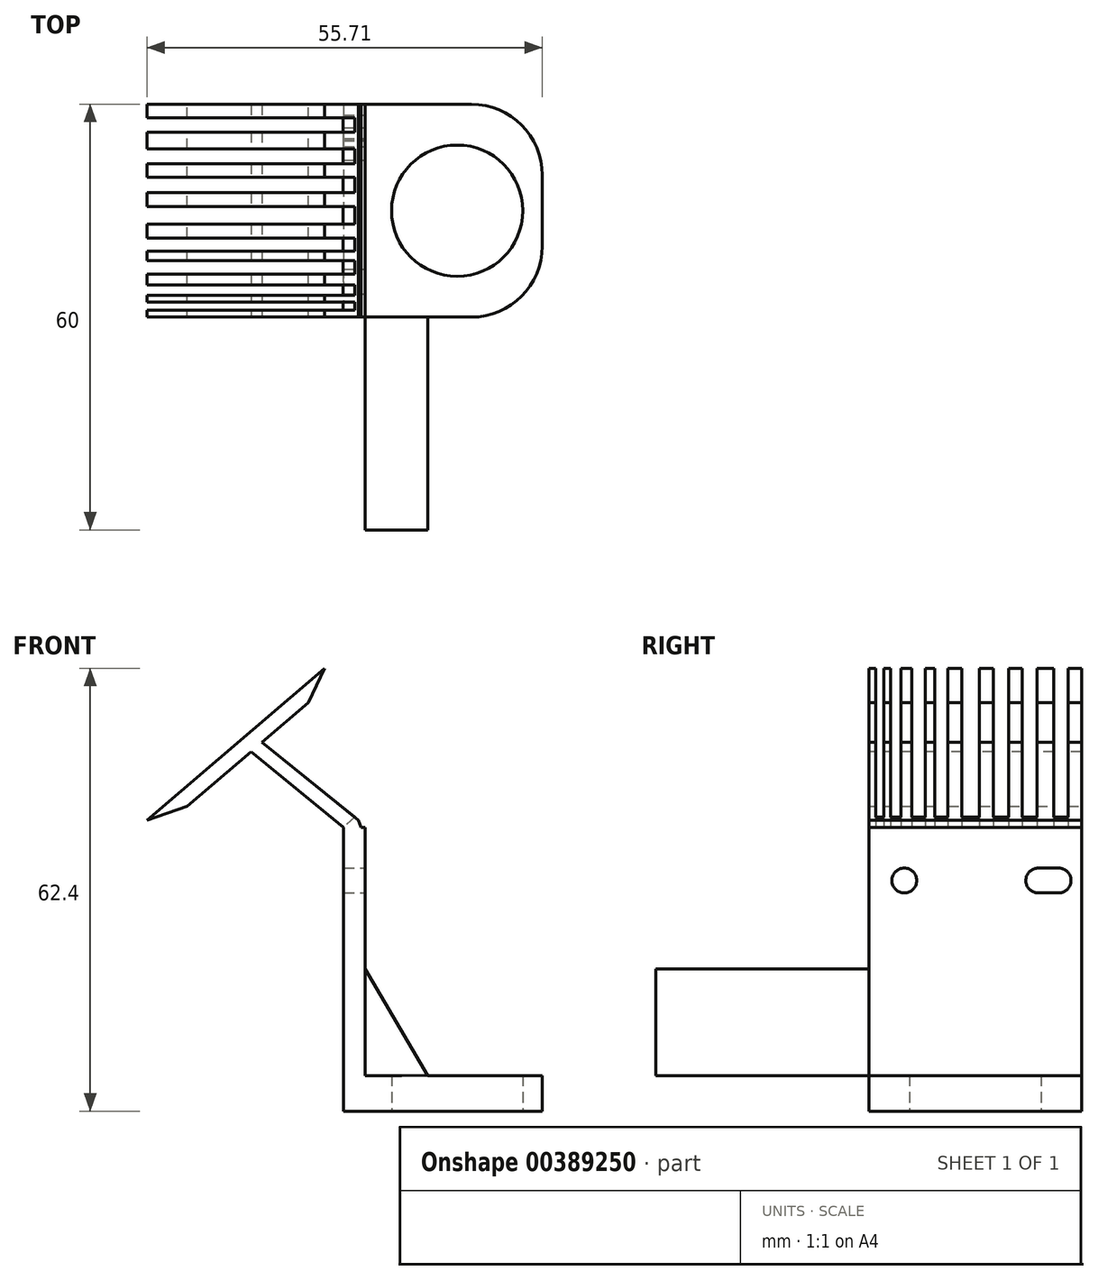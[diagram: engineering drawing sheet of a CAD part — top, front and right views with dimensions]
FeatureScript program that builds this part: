
annotation { "Feature Type Name" : "Feature", "Feature Type Description" : "" }
export const myFeature = defineFeature(function(context is Context, id is Id, definition is map)
    precondition{}
    {
        {
            var Q0;
            Q0=qCreatedBy(makeId("Top.planeOp"),FACE);
            var sketch = newSketch(context, id + "F0", { "sketchPlane" : qUnion([Q0])});
            skLineSegment(sketch, "E0.bottom", {"start": v(0, 0) * mm, "end": v(-28, 0) * mm});
            skLineSegment(sketch, "E0.top", {"start": v(0, 30) * mm, "end": v(-28, 30) * mm});
            skLineSegment(sketch, "E0.left", {"start": v(0, 0) * mm, "end": v(0, 30) * mm});
            skLineSegment(sketch, "E0.right", {"start": v(-28, 0) * mm, "end": v(-28, 30) * mm});
            skLineSegment(sketch, "E1", {"start": v(-25, 30) * mm, "end": v(-25, 0) * mm});
            skCircle(sketch, "E2", {"center": v(-12, 15) * mm, "radius": 9.25 * mm});
            skSolve(sketch);
        }
        {
            var Q0;
            Q0=qSketchRegion(id+"F0",true);
            extrude(context, id + "F1", {"entities" : qUnion([Q0]), "depth" : 5 * mm});
        }
        {
            var Q0;
            {var subQ0=sQuery(id+"F0.wireOp",EDGE,"E0.right");Q0=makeQuery(id+"F0.imprint","IMPRINT",FACE,{"disambiguationData":[TD([[makeQuery(id+"F0.imprint","IMPRINT",EDGE,{"derivedFrom":subQ0}),-1.0]])]});}
            extrude(context, id + "F2", {"entities" : qUnion([Q0]), "operationType" : NewBodyOperationType.ADD, "depth" : 40 * mm});
        }
        {
            var Q0;
            Q0=makeQuery(id+"F1.opExtrude","SWEPT_EDGE",EDGE,{"disambiguationData":[OSD([sQuery(id+"F0.wireOp",EDGE,"E0.bottom"),sQuery(id+"F0.wireOp",EDGE,"E0.left")])]});
            var Q1;
            Q1=makeQuery(id+"F1.opExtrude","SWEPT_EDGE",EDGE,{"disambiguationData":[OSD([sQuery(id+"F0.wireOp",EDGE,"E0.top"),sQuery(id+"F0.wireOp",EDGE,"E0.left")])]});
            fillet(context, id + "F3", {"entities" : qUnion([Q0, Q1]), "radius" : 10 * mm, "tangentPropagation" : true, "allowEdgeOverflow" : false});
        }
        {
            var Q0;
            Q0=makeQuery(id+"F2.opExtrude","SWEPT_FACE",FACE,{"disambiguationData":[OSD([sQuery(id+"F0.wireOp",EDGE,"E1")])]});
            var sketch = newSketch(context, id + "F4", { "sketchPlane" : qUnion([Q0])});
            skLineSegment(sketch, "E3", {"start": v(0, 32.5) * mm, "end": v(30, 32.5) * mm, "construction": true});
            skCircle(sketch, "E4", {"center": v(5, 32.5) * mm, "radius": 1.75 * mm});
            skCircle(sketch, "E5", {"center": v(25, 32.5) * mm, "radius": 1.75 * mm});
            skCircle(sketch, "E6", {"center": v(23.88, 32.5) * mm, "radius": 1.75 * mm});
            skCircle(sketch, "E7", {"center": v(26.75, 32.5) * mm, "radius": 1.75 * mm});
            skLineSegment(sketch, "E8", {"start": v(23.69, 34.24) * mm, "end": v(26.75, 34.25) * mm});
            skLineSegment(sketch, "E9", {"start": v(26.83, 30.75) * mm, "end": v(23.88, 30.75) * mm});
            skSolve(sketch);
        }
        {
            var Q0;
            Q0=qSketchRegion(id+"F4",true);
            var Q1;
            {var subQ0=sQuery(id+"F4.wireOp",EDGE,"E7");var subQ1=sQuery(id+"F4.wireOp",EDGE,"E5");var subQ2=makeQuery(id+"F4.imprint","INTERSECT",VERTEX,{"disambiguationData":[OD(0.0)],"derivedFrom":[subQ1,subQ0]});Q1=makeQuery(id+"F4.imprint","IMPRINT",FACE,{"disambiguationData":[TD([[makeQuery(id+"F4.imprint","IMPRINT",EDGE,{"disambiguationData":[TD([[subQ2,1.0]])],"derivedFrom":subQ1}),1.0]])]});}
            var Q2;
            {var subQ0=sQuery(id+"F4.wireOp",EDGE,"E6");var subQ1=sQuery(id+"F4.wireOp",EDGE,"E5");var subQ2=makeQuery(id+"F4.imprint","INTERSECT",VERTEX,{"disambiguationData":[OD(0.0)],"derivedFrom":[subQ1,subQ0]});Q2=makeQuery(id+"F4.imprint","IMPRINT",FACE,{"disambiguationData":[TD([[makeQuery(id+"F4.imprint","IMPRINT",EDGE,{"disambiguationData":[TD([[subQ2,-1.0]])],"derivedFrom":subQ1}),1.0]])]});}
            var Q3;
            {var subQ0=sQuery(id+"F4.wireOp",EDGE,"E7");var subQ1=sQuery(id+"F4.wireOp",EDGE,"E6");var subQ2=makeQuery(id+"F4.imprint","INTERSECT",VERTEX,{"disambiguationData":[OD(0.0)],"derivedFrom":[subQ1,subQ0]});Q3=makeQuery(id+"F4.imprint","IMPRINT",FACE,{"disambiguationData":[TD([[makeQuery(id+"F4.imprint","IMPRINT",EDGE,{"disambiguationData":[TD([[subQ2,1.0]])],"derivedFrom":subQ1}),1.0]])]});}
            extrude(context, id + "F5", {"entities" : qUnion([Q0, Q1, Q2, Q3]), "operationType" : NewBodyOperationType.REMOVE, "endBound" : BoundingType.THROUGH_ALL, "oppositeDirection" : true, "depth" : 25 * mm});
        }
        {
            var Q0;
            Q0=qCreatedBy(makeId("Front.planeOp"),FACE);
            var sketch = newSketch(context, id + "F6", { "sketchPlane" : qUnion([Q0])});
            skLineSegment(sketch, "E10", {"start": v(-30.69, 62.4) * mm, "end": v(-55.71, 40.97) * mm});
            skLineSegment(sketch, "E11", {"start": v(-55.71, 40.97) * mm, "end": v(-54.29, 39.3) * mm});
            skLineSegment(sketch, "E12", {"start": v(-54.29, 39.3) * mm, "end": v(-29.5, 60.53) * mm});
            skLineSegment(sketch, "E13", {"start": v(-29.5, 60.53) * mm, "end": v(-30.69, 62.4) * mm});
            skLineSegment(sketch, "E14", {"start": v(-39.52, 51.96) * mm, "end": v(-25.9, 40.97) * mm});
            skLineSegment(sketch, "E15", {"start": v(-28.04, 39.98) * mm, "end": v(-41.04, 50.65) * mm});
            skLineSegment(sketch, "E16", {"start": v(-25.9, 40.97) * mm, "end": v(-25.54, 39.97) * mm});
            skLineSegment(sketch, "E17", {"start": v(-28.04, 39.98) * mm, "end": v(-25.54, 39.98) * mm});
            skSolve(sketch);
        }
        {
            var Q0;
            {var subQ1=sQuery(id+"F6.wireOp",EDGE,"E14");Q0=makeQuery(id+"F6.imprint","IMPRINT",FACE,{"disambiguationData":[TD([[makeQuery(id+"F6.imprint","IMPRINT",EDGE,{"derivedFrom":subQ1}),-1.0]])]});}
            var Q1;
            Q1=makeQuery(id+"F6.imprint","IMPRINT",FACE,{"disambiguationData":[TD([[makeQuery(id+"F6.imprint","IMPRINT",EDGE,{"derivedFrom":sQuery(id+"F6.wireOp",EDGE,"E10")}),1.0]])]});
            extrude(context, id + "F7", {"entities" : qUnion([Q0, Q1]), "operationType" : NewBodyOperationType.ADD, "oppositeDirection" : true, "depth" : 30 * mm});
        }
        {
            var Q0;
            Q0=makeQuery(id+"F7.opExtrude","SWEPT_FACE",FACE,{"disambiguationData":[OSD([sQuery(id+"F6.wireOp",EDGE,"E10")])]});
            var sketch = newSketch(context, id + "F8", { "sketchPlane" : qUnion([Q0])});
            skLineSegment(sketch, "E18.bottom", {"start": v(17.28, 28.07) * mm, "end": v(-15.67, 28.07) * mm});
            skLineSegment(sketch, "E18.top", {"start": v(17.28, 26.07) * mm, "end": v(-15.67, 26.07) * mm});
            skLineSegment(sketch, "E18.left", {"start": v(17.28, 28.07) * mm, "end": v(17.28, 26.07) * mm});
            skLineSegment(sketch, "E18.right", {"start": v(-15.67, 28.07) * mm, "end": v(-15.67, 26.07) * mm});
            skLineSegment(sketch, "E19.bottom", {"start": v(17.28, 23.7) * mm, "end": v(-15.67, 23.7) * mm});
            skLineSegment(sketch, "E19.top", {"start": v(17.28, 21.63) * mm, "end": v(-15.67, 21.63) * mm});
            skLineSegment(sketch, "E19.left", {"start": v(17.28, 23.7) * mm, "end": v(17.28, 21.63) * mm});
            skLineSegment(sketch, "E19.right", {"start": v(-15.67, 23.7) * mm, "end": v(-15.67, 21.63) * mm});
            skLineSegment(sketch, "E20.bottom", {"start": v(17.28, 19.73) * mm, "end": v(-15.67, 19.73) * mm});
            skLineSegment(sketch, "E20.top", {"start": v(17.28, 17.54) * mm, "end": v(-15.67, 17.54) * mm});
            skLineSegment(sketch, "E20.left", {"start": v(17.28, 19.73) * mm, "end": v(17.28, 17.54) * mm});
            skLineSegment(sketch, "E20.right", {"start": v(-15.67, 19.73) * mm, "end": v(-15.67, 17.54) * mm});
            skLineSegment(sketch, "E21.bottom", {"start": v(17.28, 15.59) * mm, "end": v(-15.67, 15.59) * mm});
            skLineSegment(sketch, "E21.top", {"start": v(17.28, 13.13) * mm, "end": v(-15.67, 13.13) * mm});
            skLineSegment(sketch, "E21.left", {"start": v(17.28, 15.59) * mm, "end": v(17.28, 13.13) * mm});
            skLineSegment(sketch, "E21.right", {"start": v(-15.67, 15.59) * mm, "end": v(-15.67, 13.13) * mm});
            skLineSegment(sketch, "E22.bottom", {"start": v(17.28, 11.17) * mm, "end": v(-15.67, 11.17) * mm});
            skLineSegment(sketch, "E22.top", {"start": v(17.28, 9.27) * mm, "end": v(-15.67, 9.27) * mm});
            skLineSegment(sketch, "E22.left", {"start": v(17.28, 11.17) * mm, "end": v(17.28, 9.27) * mm});
            skLineSegment(sketch, "E22.right", {"start": v(-15.67, 11.17) * mm, "end": v(-15.67, 9.27) * mm});
            skLineSegment(sketch, "E23.bottom", {"start": v(17.28, 7.98) * mm, "end": v(-15.67, 7.98) * mm});
            skLineSegment(sketch, "E23.top", {"start": v(17.28, 6.08) * mm, "end": v(-15.67, 6.08) * mm});
            skLineSegment(sketch, "E23.left", {"start": v(17.28, 7.98) * mm, "end": v(17.28, 6.08) * mm});
            skLineSegment(sketch, "E23.right", {"start": v(-15.67, 7.98) * mm, "end": v(-15.67, 6.08) * mm});
            skLineSegment(sketch, "E24.bottom", {"start": v(17.28, 4.51) * mm, "end": v(-15.67, 4.51) * mm});
            skLineSegment(sketch, "E24.top", {"start": v(17.28, 3.06) * mm, "end": v(-15.67, 3.06) * mm});
            skLineSegment(sketch, "E24.left", {"start": v(17.28, 4.51) * mm, "end": v(17.28, 3.06) * mm});
            skLineSegment(sketch, "E24.right", {"start": v(-15.67, 4.51) * mm, "end": v(-15.67, 3.06) * mm});
            skLineSegment(sketch, "E25.bottom", {"start": v(17.28, 2.1) * mm, "end": v(-15.67, 2.1) * mm});
            skLineSegment(sketch, "E25.top", {"start": v(17.28, 0.99) * mm, "end": v(-15.67, 0.99) * mm});
            skLineSegment(sketch, "E25.left", {"start": v(17.28, 2.1) * mm, "end": v(17.28, 0.99) * mm});
            skLineSegment(sketch, "E25.right", {"start": v(-15.67, 2.1) * mm, "end": v(-15.67, 0.99) * mm});
            skSolve(sketch);
        }
        {
            var Q0;
            Q0=makeQuery(id+"F8.imprint","IMPRINT",FACE,{"disambiguationData":[TD([[makeQuery(id+"F8.imprint","IMPRINT",EDGE,{"derivedFrom":sQuery(id+"F8.wireOp",EDGE,"E18.bottom")}),1.0]])]});
            var Q1;
            Q1=makeQuery(id+"F8.imprint","IMPRINT",FACE,{"disambiguationData":[TD([[makeQuery(id+"F8.imprint","IMPRINT",EDGE,{"derivedFrom":sQuery(id+"F8.wireOp",EDGE,"E19.bottom")}),1.0]])]});
            var Q2;
            Q2=makeQuery(id+"F8.imprint","IMPRINT",FACE,{"disambiguationData":[TD([[makeQuery(id+"F8.imprint","IMPRINT",EDGE,{"derivedFrom":sQuery(id+"F8.wireOp",EDGE,"E20.bottom")}),1.0]])]});
            var Q3;
            Q3=makeQuery(id+"F8.imprint","IMPRINT",FACE,{"disambiguationData":[TD([[makeQuery(id+"F8.imprint","IMPRINT",EDGE,{"derivedFrom":sQuery(id+"F8.wireOp",EDGE,"E21.bottom")}),1.0]])]});
            var Q4;
            Q4=makeQuery(id+"F8.imprint","IMPRINT",FACE,{"disambiguationData":[TD([[makeQuery(id+"F8.imprint","IMPRINT",EDGE,{"derivedFrom":sQuery(id+"F8.wireOp",EDGE,"E22.bottom")}),1.0]])]});
            var Q5;
            Q5=makeQuery(id+"F8.imprint","IMPRINT",FACE,{"disambiguationData":[TD([[makeQuery(id+"F8.imprint","IMPRINT",EDGE,{"derivedFrom":sQuery(id+"F8.wireOp",EDGE,"E23.bottom")}),1.0]])]});
            var Q6;
            Q6=makeQuery(id+"F8.imprint","IMPRINT",FACE,{"disambiguationData":[TD([[makeQuery(id+"F8.imprint","IMPRINT",EDGE,{"derivedFrom":sQuery(id+"F8.wireOp",EDGE,"E24.bottom")}),1.0]])]});
            var Q7;
            Q7=makeQuery(id+"F8.imprint","IMPRINT",FACE,{"disambiguationData":[TD([[makeQuery(id+"F8.imprint","IMPRINT",EDGE,{"derivedFrom":sQuery(id+"F8.wireOp",EDGE,"E25.bottom")}),1.0]])]});
            extrude(context, id + "F9", {"entities" : qUnion([Q0, Q1, Q2, Q3, Q4, Q5, Q6, Q7]), "operationType" : NewBodyOperationType.REMOVE, "oppositeDirection" : true, "depth" : 18.7 * mm});
        }
        {
            var Q0;
            {var subQ0=sQuery(id+"F0.wireOp",EDGE,"E0.top");Q0=makeQuery(id+"F7.boolean.opBoolean","MERGE",FACE,{"derivedFrom":[makeQuery(id+"F2.boolean.opBoolean","MERGE",FACE,{"derivedFrom":[makeQuery(id+"F1.opExtrude","SWEPT_FACE",FACE,{"disambiguationData":[OSD([subQ0])]}),makeQuery(id+"F2.opExtrude","SWEPT_FACE",FACE,{"disambiguationData":[OSD([subQ0])]})]}),makeQuery(id+"F7.opExtrude","CAP_FACE",FACE,{"disambiguationData":[OSD([sQuery(id+"F6.wireOp",EDGE,"E10"),sQuery(id+"F6.wireOp",EDGE,"E11"),sQuery(id+"F6.wireOp",EDGE,"E12"),sQuery(id+"F6.wireOp",EDGE,"E13"),sQuery(id+"F6.wireOp",EDGE,"E14"),sQuery(id+"F6.wireOp",EDGE,"E15"),sQuery(id+"F6.wireOp",EDGE,"E16"),sQuery(id+"F6.wireOp",EDGE,"E17")])],"isStart":false})]});}
            var sketch = newSketch(context, id + "F10", { "sketchPlane" : qUnion([Q0])});
            skLineSegment(sketch, "E26", {"start": v(30.69, 62.4) * mm, "end": v(32.98, 57.55) * mm});
            skLineSegment(sketch, "E27", {"start": v(32.98, 57.55) * mm, "end": v(29.5, 60.53) * mm});
            skLineSegment(sketch, "E28", {"start": v(29.5, 60.53) * mm, "end": v(30.69, 62.4) * mm});
            skLineSegment(sketch, "E29", {"start": v(54.29, 39.3) * mm, "end": v(55.71, 40.97) * mm});
            skLineSegment(sketch, "E30", {"start": v(55.71, 40.97) * mm, "end": v(50.05, 42.94) * mm});
            skLineSegment(sketch, "E31", {"start": v(50.05, 42.94) * mm, "end": v(54.29, 39.3) * mm});
            skSolve(sketch);
        }
        {
            var Q0;
            Q0 = qSketchRegion(id + "F10", true);
            extrude(context, id + "F11", {"entities" : qUnion([Q0]), "operationType" : NewBodyOperationType.REMOVE, "endBound" : BoundingType.THROUGH_ALL, "oppositeDirection" : true, "depth" : 25 * mm});
        }
        {
            var Q0;
            Q0=qCreatedBy(makeId("Front.planeOp"),FACE);
            var sketch = newSketch(context, id + "F12", { "sketchPlane" : qUnion([Q0])});
            skLineSegment(sketch, "E32", {"start": v(-24.97, 5.04) * mm, "end": v(-24.97, 20.06) * mm});
            skLineSegment(sketch, "E33", {"start": v(-24.97, 20.06) * mm, "end": v(-16.12, 4.97) * mm});
            skLineSegment(sketch, "E34", {"start": v(-16.12, 4.97) * mm, "end": v(-24.97, 5.04) * mm});
            skSolve(sketch);
        }
        {
            var Q0;
            Q0 = qSketchRegion(id + "F12", true);
            extrude(context, id + "F13", {"entities" : qUnion([Q0]), "operationType" : NewBodyOperationType.ADD, "depth" : 30 * mm, "offsetDistance" : 25 * mm});
        }
    });
